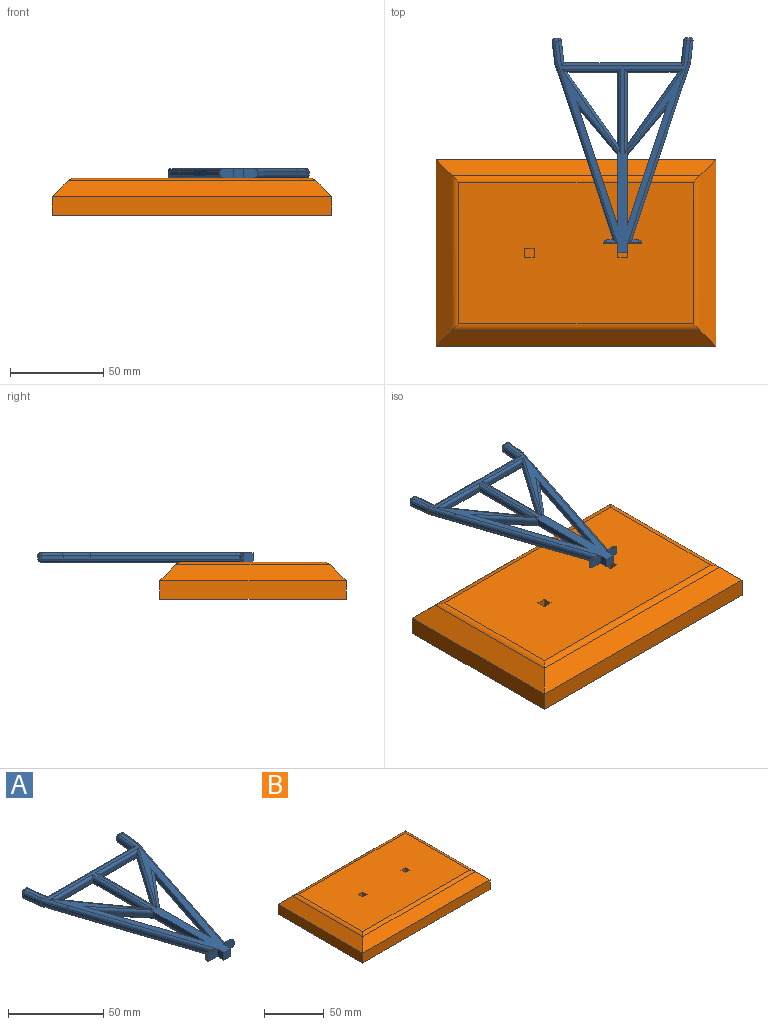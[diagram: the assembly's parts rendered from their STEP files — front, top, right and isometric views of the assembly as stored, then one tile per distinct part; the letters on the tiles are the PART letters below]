
ASSEMBLY  parts=2 mates=1
PART A: 102 faces, bbox 75.6x115.5x5 mm
  f0: plane 38.94x2mm, normal (1,0,0), area 77.9mm2, adj f1,f31,f86,f96
  f1: plane 27.34x2mm, normal (0,-1,0), area 54.7mm2, adj f0,f31,f87,f97
  f2: plane 27.34x2mm, normal (0,-1,0), area 54.7mm2, adj f3,f27,f88,f99
  f3: plane 38.94x2mm, normal (-1,0,0), area 77.9mm2, adj f2,f27,f89,f100
  f4: plane 66.53x22.06mm, normal (0.95,0.31,0), area 232.4mm2, adj f5,f28,f32,f83,f94
  f5: plane 24.74x20.78mm, normal (-0.77,-0.64,0), area 64.6mm2, adj f4,f28,f82,f94
  f6: plane 24.74x20.78mm, normal (0.77,-0.64,0), area 64.6mm2, adj f7,f29,f93,f98
  f7: plane 66.53x22.06mm, normal (-0.95,0.31,0), area 232.4mm2, adj f6,f29,f32,f91,f98
  f8: plane 11.45x2mm, normal (-0.99,-0.11,0), area 23.1mm2, adj f9,f44,f47,f48
  f9: plane 15x5mm, normal (-0.95,-0.32,0), area 31.6mm2, adj f8,f10,f42,f45
  f10: plane 80x26.5mm, normal (-0.95,-0.31,0), area 168.5mm2, adj f9,f11,f40,f43
  f11: plane 3.5x2mm, normal (0,1,0), area 7mm2, adj f10,f37,f38,f41
  f12: plane 2x0.5mm, normal (-1,0,0), area 1mm2, adj f13,f34,f36,f37
  f13: plane 7.5x5mm, normal (0,-1,0), area 36.5mm2, adj f12,f14,f32,f33,f34,f36
  f14: plane 5x5mm, normal (-1,0,0), area 25mm2, adj f13,f15,f32,f33
  f15: plane 5x5mm, normal (0,-1,0), area 25mm2, adj f14,f16,f32,f33
  f16: plane 5x5mm, normal (1,0,0), area 25mm2, adj f15,f17,f32,f33
  f17: plane 7.5x5mm, normal (0,-1,0), area 36.5mm2, adj f16,f18,f32,f33,f61,f71
  f18: plane 2x0.5mm, normal (1,0,0), area 1mm2, adj f17,f61,f70,f71
  f19: plane 3.5x2mm, normal (0,1,0), area 7mm2, adj f20,f60,f70,f77
  f20: plane 80x26.5mm, normal (0.95,-0.31,0), area 168.5mm2, adj f19,f21,f59,f79
  f21: plane 15x5mm, normal (0.95,-0.32,0), area 31.6mm2, adj f20,f22,f64,f81
  f22: plane 11.83x2mm, normal (0.99,-0.11,0), area 23.8mm2, adj f21,f69,f76,f80
  f23: plane 2x1.98mm, normal (0,1,0), area 4mm2, adj f67,f68,f75,f76
  f24: plane 12.17x2mm, normal (-0.99,0.11,0), area 24.5mm2, adj f25,f58,f66,f67
  f25: plane 63x2mm, normal (0,1,0), area 126mm2, adj f24,f26,f56,f62
  f26: plane 12.01x2mm, normal (0.99,0.11,0), area 24.2mm2, adj f25,f53,f54,f57
  f27: plane 38.94x27.34mm, normal (0.82,0.57,0), area 95.2mm2, adj f2,f3,f90,f101
  f28: plane 40.27x3.5mm, normal (-1,0,0), area 133.5mm2, adj f4,f5,f32,f84,f94
  f29: plane 40.27x3.5mm, normal (1,0,0), area 133.5mm2, adj f6,f7,f32,f92,f98
  f30: plane 2x1.98mm, normal (-0.11,0.99,0), area 4mm2, adj f48,f49,f52,f53
  f31: plane 38.94x27.34mm, normal (-0.82,0.57,0), area 95.2mm2, adj f0,f1,f85,f95
  f32: plane 114x72.63mm, normal (0,0,1), area 1309.1mm2, adj f4,f7,f13,f14,f15,f16,f17,f28
  f33: plane 114x72.63mm, normal (0,0,-1), area 947.2mm2, adj f13,f14,f15,f16,f17,f34,f38,f40
  f34: cylinder r=1.5mm len=1.5mm, axis (0,-1,0), area 1.2mm2, adj f12,f13,f33,f35
  f35: sphere r=1.5mm, area 3.5mm2, adj f34,f37,f38
  f36: cylinder r=1.5mm len=1.5mm, axis (0,1,0), area 1.2mm2, adj f12,f13,f32,f39
  f37: cylinder r=1.5mm len=2mm, axis (0,0,1), area 4.7mm2, adj f11,f12,f35,f39
  f38: cylinder r=1.5mm len=5.58mm, axis (-1,0,0), area 10mm2, adj f11,f33,f35,f40
  f39: sphere r=1.5mm, area 3.5mm2, adj f36,f37,f41
  f40: cylinder r=1.5mm len=82.44mm, axis (0.31,-0.95,0), area 200.3mm2, adj f10,f33,f38,f42
  f41: cylinder r=1.5mm len=5.58mm, axis (1,0,0), area 10mm2, adj f11,f32,f39,f43
  f42: cylinder r=1.5mm len=15.48mm, axis (0.32,-0.95,0), area 37.1mm2, adj f9,f33,f40,f44
  f43: cylinder r=1.5mm len=82.45mm, axis (-0.31,0.95,0), area 200.3mm2, adj f10,f32,f41,f45
  f44: cylinder r=1.5mm len=11.62mm, axis (0.11,-0.99,0), area 27mm2, adj f8,f33,f42,f46
  f45: cylinder r=1.5mm len=15.47mm, axis (-0.32,0.95,0), area 37.1mm2, adj f9,f32,f43,f47
  f46: sphere r=1.5mm, area 3.5mm2, adj f44,f48,f49
  f47: cylinder r=1.5mm len=11.62mm, axis (-0.11,0.99,0), area 27mm2, adj f8,f32,f45,f50
  f48: cylinder r=1.5mm len=2mm, axis (0,0,-1), area 4.7mm2, adj f8,f30,f46,f50
  f49: cylinder r=1.5mm len=2.15mm, axis (-0.99,-0.11,0), area 4.7mm2, adj f30,f33,f46,f51
  f50: sphere r=1.5mm, area 3.5mm2, adj f47,f48,f52
  f51: sphere r=1.5mm, area 3.5mm2, adj f49,f53,f54
  f52: cylinder r=1.5mm len=2.15mm, axis (0.99,0.11,0), area 4.7mm2, adj f30,f32,f50,f55
  f53: cylinder r=1.5mm len=2mm, axis (0,0,-1), area 4.7mm2, adj f26,f30,f51,f55
  f54: cylinder r=1.5mm len=13.51mm, axis (-0.11,0.99,0), area 29.6mm2, adj f26,f33,f51,f56
  f55: sphere r=1.5mm, area 3.5mm2, adj f52,f53,f57
  f56: cylinder r=1.5mm len=65.69mm, axis (-1,0,0), area 150.7mm2, adj f25,f33,f54,f58
  f57: cylinder r=1.5mm len=13.51mm, axis (0.11,-0.99,0), area 29.6mm2, adj f26,f32,f55,f62
  f58: cylinder r=1.5mm len=13.67mm, axis (-0.11,-0.99,0), area 30mm2, adj f24,f33,f56,f63
  f59: cylinder r=1.5mm len=82.44mm, axis (0.31,0.95,0), area 200.3mm2, adj f20,f33,f60,f64
  f60: cylinder r=1.5mm len=5.58mm, axis (-1,0,0), area 10mm2, adj f19,f33,f59,f65
  f61: cylinder r=1.5mm len=1.5mm, axis (0,1,0), area 1.2mm2, adj f17,f18,f33,f65
  f62: cylinder r=1.5mm len=65.69mm, axis (1,0,0), area 150.7mm2, adj f25,f32,f57,f66
  f63: sphere r=1.5mm, area 3.3mm2, adj f58,f67,f68
  f64: cylinder r=1.5mm len=15.48mm, axis (0.32,0.95,0), area 37.1mm2, adj f21,f33,f59,f69
  f65: sphere r=1.5mm, area 3.5mm2, adj f60,f61,f70
  f66: cylinder r=1.5mm len=13.67mm, axis (0.11,0.99,0), area 30mm2, adj f24,f32,f62,f72
  f67: cylinder r=1.5mm len=2mm, axis (0,0,-1), area 4.4mm2, adj f23,f24,f63,f72
  f68: cylinder r=1.5mm len=1.98mm, axis (-1,0,0), area 4.7mm2, adj f23,f33,f63,f73
  f69: cylinder r=1.5mm len=12mm, axis (0.11,0.99,0), area 27.9mm2, adj f22,f33,f64,f73
  f70: cylinder r=1.5mm len=2mm, axis (0,0,-1), area 4.7mm2, adj f18,f19,f65,f74
  f71: cylinder r=1.5mm len=1.5mm, axis (0,-1,0), area 1.2mm2, adj f17,f18,f32,f74
  f72: sphere r=1.5mm, area 3.3mm2, adj f66,f67,f75
  f73: sphere r=1.5mm, area 3.8mm2, adj f68,f69,f76
  f74: sphere r=1.5mm, area 3.5mm2, adj f70,f71,f77
  f75: cylinder r=1.5mm len=1.98mm, axis (1,0,0), area 4.7mm2, adj f23,f32,f72,f78
  f76: cylinder r=1.5mm len=2mm, axis (0,0,-1), area 5mm2, adj f22,f23,f73,f78
  f77: cylinder r=1.5mm len=5.58mm, axis (1,0,0), area 10mm2, adj f19,f32,f74,f79
  f78: sphere r=1.5mm, area 3.8mm2, adj f75,f76,f80
  f79: cylinder r=1.5mm len=82.44mm, axis (-0.31,-0.95,0), area 200.3mm2, adj f20,f32,f77,f81
  f80: cylinder r=1.5mm len=12mm, axis (-0.11,-0.99,0), area 27.9mm2, adj f22,f32,f78,f81
  f81: cylinder r=1.5mm len=15.48mm, axis (-0.32,-0.95,0), area 37.1mm2, adj f21,f32,f79,f80
  f82: cylinder r=1.5mm len=32.12mm, axis (0.64,-0.77,0), area 83.3mm2, adj f5,f33,f83,f84
  f83: cylinder r=1.5mm len=79.4mm, axis (-0.31,0.95,0), area 170.2mm2, adj f4,f33,f82,f84
  f84: cylinder r=1.5mm len=47.77mm, axis (0,-1,0), area 97.8mm2, adj f28,f33,f82,f83
  f85: cylinder r=1.5mm len=46.05mm, axis (-0.57,-0.82,0), area 118.6mm2, adj f31,f33,f86,f87
  f86: cylinder r=1.5mm len=45.19mm, axis (0,1,0), area 97.1mm2, adj f0,f33,f85,f87
  f87: cylinder r=1.5mm len=31.73mm, axis (1,0,0), area 68.2mm2, adj f1,f33,f85,f86
  f88: cylinder r=1.5mm len=31.73mm, axis (1,0,0), area 68.2mm2, adj f2,f33,f89,f90
  f89: cylinder r=1.5mm len=45.19mm, axis (0,-1,0), area 97.1mm2, adj f3,f33,f88,f90
  f90: cylinder r=1.5mm len=46.05mm, axis (-0.57,0.82,0), area 118.6mm2, adj f27,f33,f88,f89
  f91: cylinder r=1.5mm len=79.4mm, axis (-0.31,-0.95,0), area 170.2mm2, adj f7,f33,f92,f93
  f92: cylinder r=1.5mm len=47.77mm, axis (0,1,0), area 97.8mm2, adj f29,f33,f91,f93
  f93: cylinder r=1.5mm len=32.12mm, axis (0.64,0.77,0), area 83.3mm2, adj f6,f33,f91,f92
  f94: cylinder r=1.5mm len=28.59mm, axis (-0.64,0.77,0), area 77.8mm2, adj f4,f5,f28,f32
  f95: cylinder r=1.5mm len=46.05mm, axis (0.57,0.82,0), area 118.6mm2, adj f31,f32,f96,f97
  f96: cylinder r=1.5mm len=45.19mm, axis (0,-1,0), area 97.1mm2, adj f0,f32,f95,f97
  f97: cylinder r=1.5mm len=31.73mm, axis (-1,0,0), area 68.2mm2, adj f1,f32,f95,f96
  f98: cylinder r=1.5mm len=28.59mm, axis (-0.64,-0.77,0), area 77.8mm2, adj f6,f7,f29,f32
  f99: cylinder r=1.5mm len=31.73mm, axis (-1,0,0), area 68.2mm2, adj f2,f32,f100,f101
  f100: cylinder r=1.5mm len=45.19mm, axis (0,1,0), area 97.1mm2, adj f3,f32,f99,f101
  f101: cylinder r=1.5mm len=46.05mm, axis (0.57,-0.82,0), area 118.6mm2, adj f27,f32,f99,f100
PART B: 24 faces, bbox 150x100x20 mm
  f0: plane 125.86x75.86mm, normal (0,0,1), area 9497.3mm2, adj f10,f11,f12,f13,f15,f16,f17,f18
  f1: plane 150x10mm, normal (0,1,0), area 1500mm2, adj f2,f4,f5,f7
  f2: plane 100x10mm, normal (-1,0,0), area 1000mm2, adj f1,f3,f5,f6
  f3: plane 150x10mm, normal (0,-1,0), area 1500mm2, adj f2,f4,f5,f8
  f4: plane 100x10mm, normal (1,0,0), area 1000mm2, adj f1,f3,f5,f9
  f5: plane 150x100mm, normal (0,0,-1), area 15000mm2, adj f1,f2,f3,f4
  f6: plane 100x8.54mm, normal (-0.71,0,0.71), area 1104.1mm2, adj f2,f7,f8,f20
  f7: plane 150x8.54mm, normal (0,0.71,0.71), area 1707.6mm2, adj f1,f6,f9,f22
  f8: plane 150x8.54mm, normal (0,-0.71,0.71), area 1707.6mm2, adj f3,f6,f9,f21
  f9: plane 100x8.54mm, normal (0.71,0,0.71), area 1104.1mm2, adj f4,f7,f8,f23
  f10: plane 10x5mm, normal (0,-1,0), area 50mm2, adj f0,f11,f13,f14
  f11: plane 10x5mm, normal (1,0,0), area 50mm2, adj f0,f10,f12,f14
  f12: plane 10x5mm, normal (0,1,0), area 50mm2, adj f0,f11,f13,f14
  f13: plane 10x5mm, normal (-1,0,0), area 50mm2, adj f0,f10,f12,f14
  f14: plane 5x5mm, normal (0,0,1), area 25mm2, adj f10,f11,f12,f13
  f15: plane 10x5mm, normal (0,1,0), area 50mm2, adj f0,f16,f18,f19
  f16: plane 10x5mm, normal (-1,0,0), area 50mm2, adj f0,f15,f17,f19
  f17: plane 10x5mm, normal (0,-1,0), area 50mm2, adj f0,f16,f18,f19
  f18: plane 10x5mm, normal (1,0,0), area 50mm2, adj f0,f15,f17,f19
  f19: plane 5x5mm, normal (0,0,1), area 25mm2, adj f15,f16,f17,f18
  f20: cylinder r=5mm len=82.93mm, axis (0,-1,0), area 312.5mm2, adj f0,f6,f21,f22
  f21: cylinder r=5mm len=132.93mm, axis (1,0,0), area 508.9mm2, adj f0,f8,f20,f23
  f22: cylinder r=5mm len=132.93mm, axis (1,0,0), area 508.9mm2, adj f0,f7,f20,f23
  f23: cylinder r=5mm len=82.93mm, axis (0,-1,0), area 312.5mm2, adj f0,f9,f21,f22
PLACE A t=(-0.05,81,7.77)mm
PLACE B t=(-42.92,29,-12.23)mm
MATE slider A.f33 <-> B.f0  axis (0,0,1) through (-11.29,-21,7.77)mm
